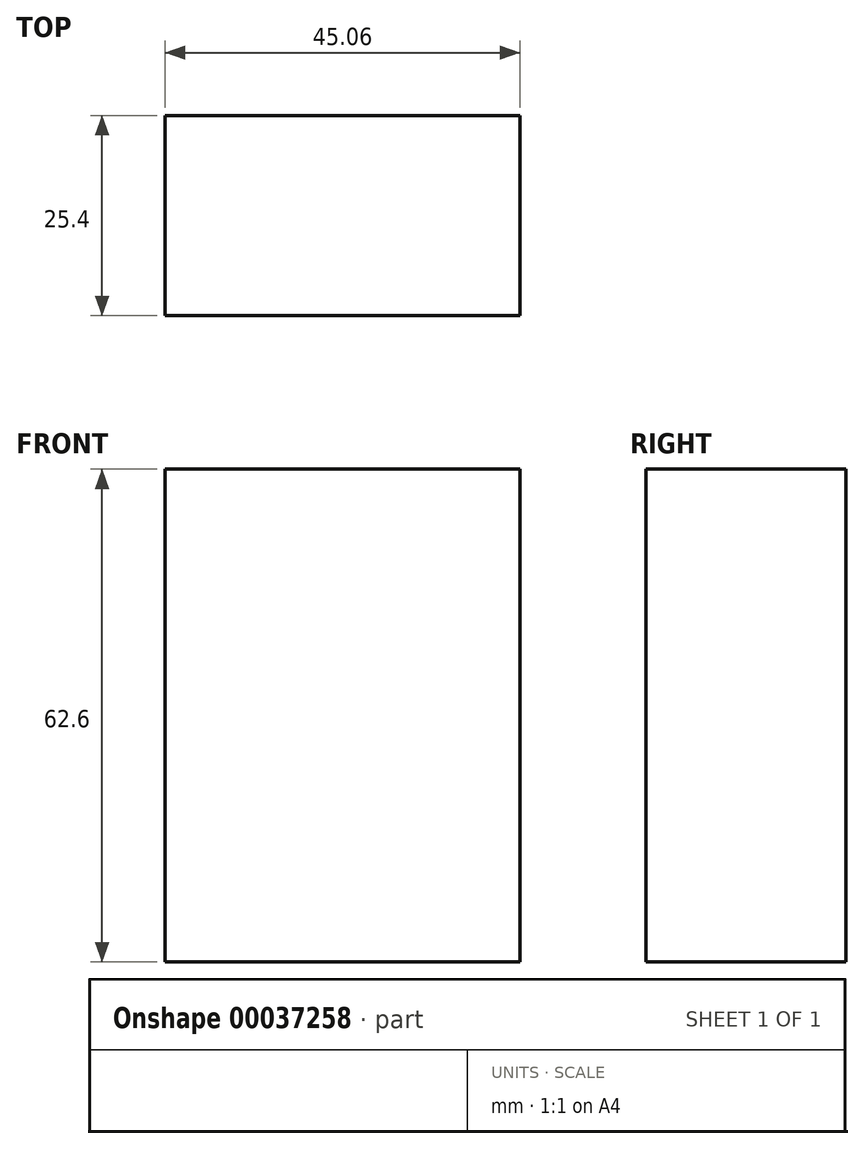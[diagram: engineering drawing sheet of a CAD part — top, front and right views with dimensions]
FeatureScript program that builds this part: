
annotation { "Feature Type Name" : "Feature", "Feature Type Description" : "" }
export const myFeature = defineFeature(function(context is Context, id is Id, definition is map)
    precondition{}
    {
        {
            var Q0;
            Q0=qCreatedBy(makeId("Front.planeOp"),FACE);
            var sketch = newSketch(context, id + "F0", { "sketchPlane" : qUnion([Q0])});
            skLineSegment(sketch, "E0.rect.bottom", {"start": v(-22.53, 31.3) * mm, "end": v(22.53, 31.3) * mm});
            skLineSegment(sketch, "E0.rect.top", {"start": v(-22.53, -31.3) * mm, "end": v(22.53, -31.3) * mm});
            skLineSegment(sketch, "E0.rect.left", {"start": v(-22.53, 31.3) * mm, "end": v(-22.53, -31.3) * mm});
            skLineSegment(sketch, "E0.rect.right", {"start": v(22.53, 31.3) * mm, "end": v(22.53, -31.3) * mm});
            skPoint(sketch, "E0.rect.middle", {"position": v(0, 0) * mm});
            skLineSegment(sketch, "E1", {"start": v(0, 31.3) * mm, "end": v(0, -31.3) * mm});
            skSolve(sketch);
        }
        {
            var Q0;
            {var subQ1=sQuery(id+"F0.wireOp",EDGE,"E0.rect.left");Q0=makeQuery(id+"F0.imprint","IMPRINT",FACE,{"disambiguationData":[TD([[makeQuery(id+"F0.imprint","IMPRINT",EDGE,{"derivedFrom":subQ1}),1.0]])]});}
            var Q1;
            {var subQ1=sQuery(id+"F0.wireOp",EDGE,"E0.rect.right");Q1=makeQuery(id+"F0.imprint","IMPRINT",FACE,{"disambiguationData":[TD([[makeQuery(id+"F0.imprint","IMPRINT",EDGE,{"derivedFrom":subQ1}),-1.0]])]});}
            extrude(context, id + "F1", {"entities" : qUnion([Q0, Q1]), "depth" : 25.4 * mm});
        }
    });
